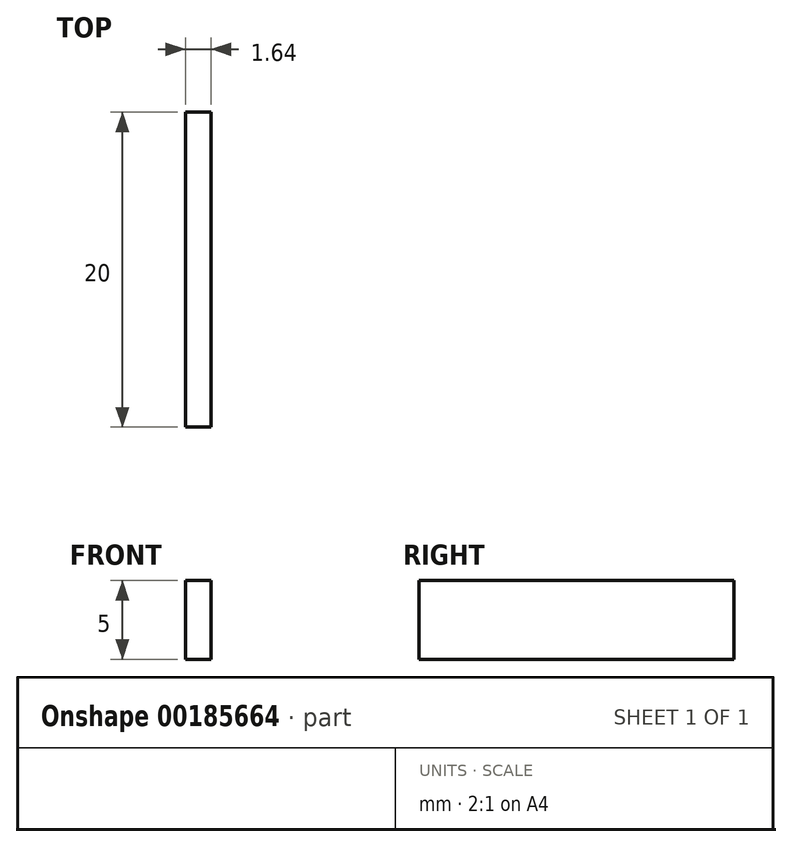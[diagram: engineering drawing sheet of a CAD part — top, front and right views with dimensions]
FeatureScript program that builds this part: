
annotation { "Feature Type Name" : "Feature", "Feature Type Description" : "" }
export const myFeature = defineFeature(function(context is Context, id is Id, definition is map)
    precondition{}
    {
        {
            var Q0;
            Q0=qCreatedBy(makeId("Top.planeOp"),FACE);
            var sketch = newSketch(context, id + "F0", { "sketchPlane" : qUnion([Q0])});
            skLineSegment(sketch, "E0.bottom", {"start": v(0.83, 10) * mm, "end": v(-0.82, 10) * mm});
            skLineSegment(sketch, "E0.top", {"start": v(0.82, -10) * mm, "end": v(-0.83, -10) * mm});
            skLineSegment(sketch, "E0.left", {"start": v(0.83, 10) * mm, "end": v(0.82, -10) * mm});
            skLineSegment(sketch, "E0.right", {"start": v(-0.82, 10) * mm, "end": v(-0.83, -10) * mm});
            skPoint(sketch, "E0.middle", {"position": v(0, 0) * mm});
            skSolve(sketch);
        }
        {
            var Q0;
            Q0=makeQuery(id+"F0.imprint","IMPRINT",FACE,{"disambiguationData":[TD([[makeQuery(id+"F0.imprint","IMPRINT",EDGE,{"derivedFrom":sQuery(id+"F0.wireOp",EDGE,"E0.bottom")}),1.0]])]});
            extrude(context, id + "F1", {"entities" : qUnion([Q0]), "depth" : 5 * mm});
        }
    });
